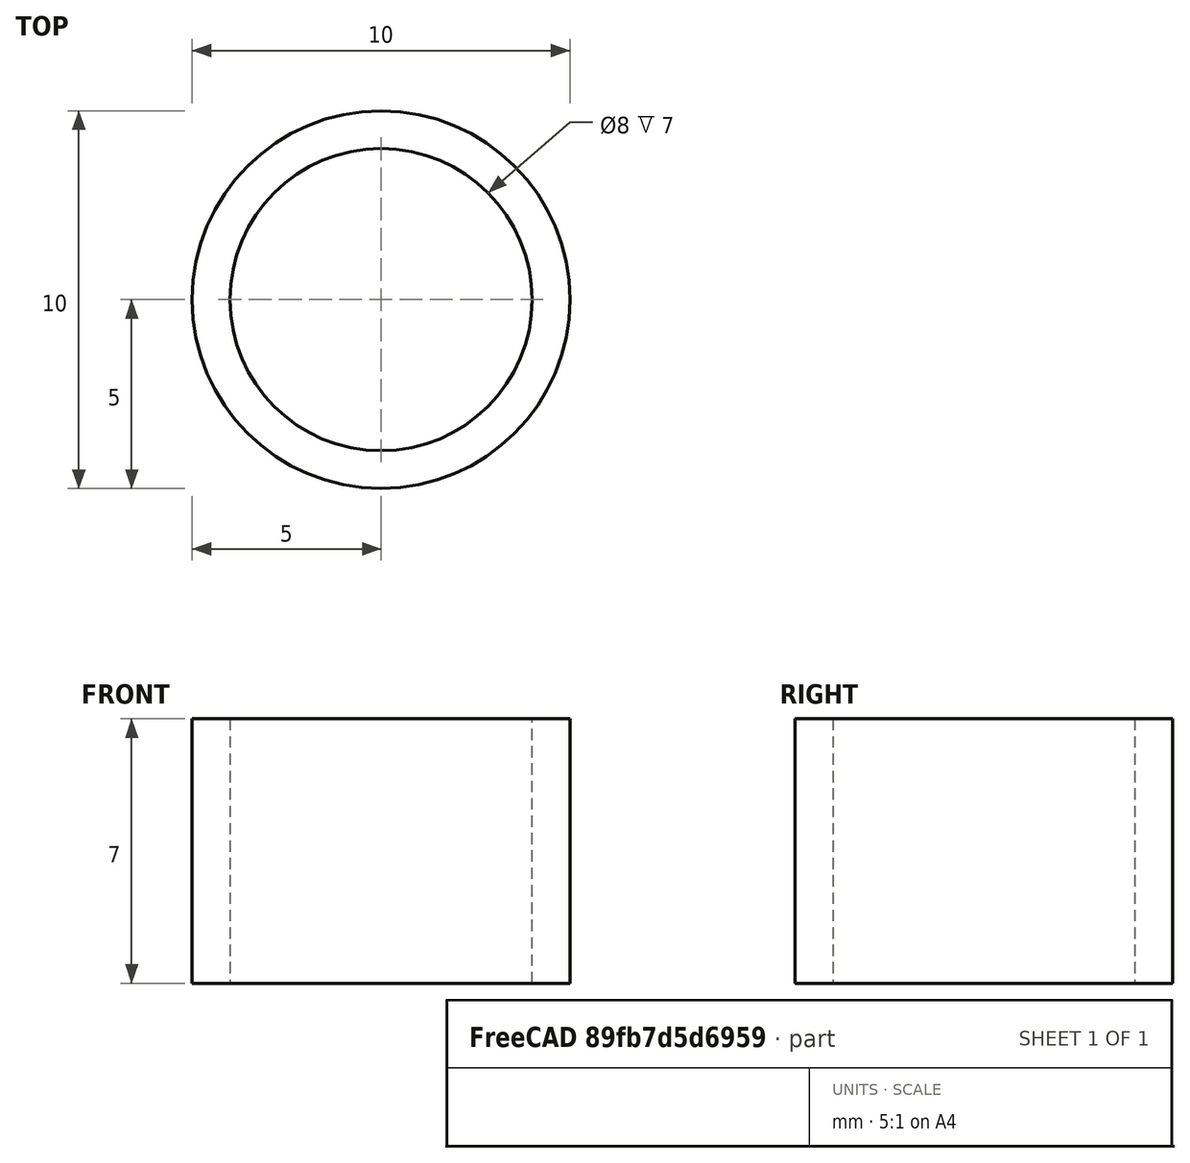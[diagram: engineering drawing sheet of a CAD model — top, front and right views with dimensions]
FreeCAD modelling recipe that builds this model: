
FCSTD DOCUMENT  (FreeCAD 0.19R24276 (Git))
Label: podshipnik_22x8x7_in_ring
License: All rights reserved
LicenseURL: http://en.wikipedia.org/wiki/All_rights_reserved
objects: Sketcher::SketchObject×1, PartDesign::Pad×1, PartDesign::Body×1
note: 4 computed .brp shape members not serialized (recipe doc carries the construction recipe); baked Part::Feature solids carry a one-line shape summary decoded from their .brp

FEATURE [Sketcher::SketchObject] Sketch
  FullyConstrained = true
  MapMode = 5
  Support = -> [XY_Plane]
  sketch-geometry (2):
    g0: Circle CenterX=0 CenterY=0 CenterZ=0 NormalX=0 NormalY=0 NormalZ=1 AngleXU=0 Radius=4
    g1: Circle CenterX=0 CenterY=0 CenterZ=0 NormalX=0 NormalY=0 NormalZ=1 AngleXU=0 Radius=5
  constraints (4):
    c: Coincident(g0,g-1)
    c: Coincident(g1,g0)
    c: Diameter(g0) = 8
    c: Diameter(g1) = 10
FEATURE [PartDesign::Pad] Pad
  Direction = (1,1,1)
  Length = 7
  Length2 = 100
  Profile = -> Sketch
  Type = 0
FEATURE [PartDesign::Body] Body
  Group = -> [Sketch,Pad]
  Origin = -> Origin
  Tip = -> Pad
